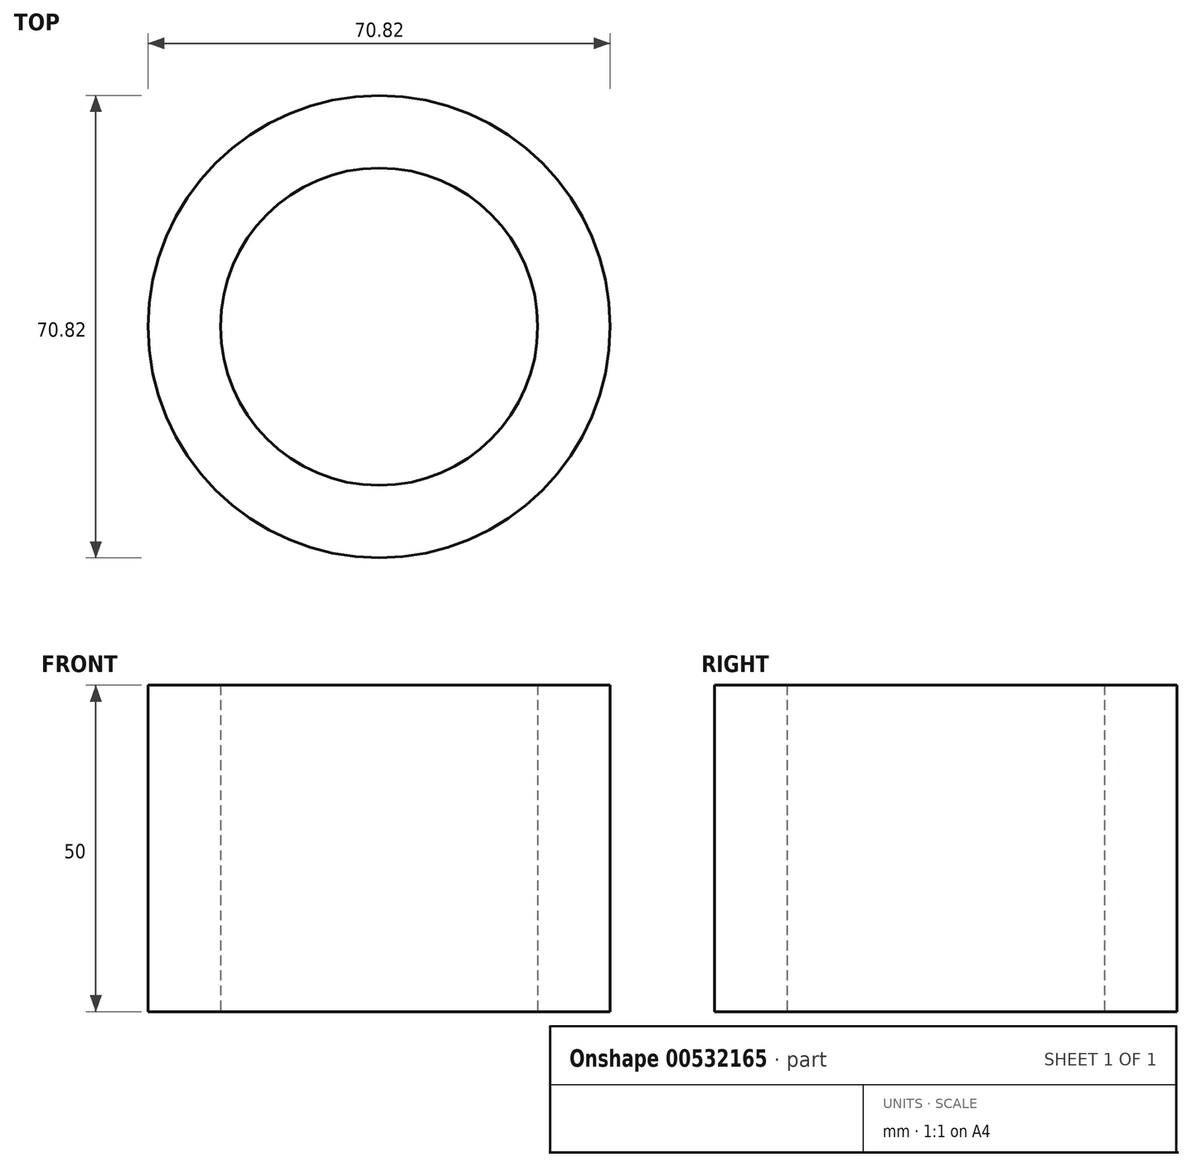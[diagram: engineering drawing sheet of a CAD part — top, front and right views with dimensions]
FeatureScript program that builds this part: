
annotation { "Feature Type Name" : "Feature", "Feature Type Description" : "" }
export const myFeature = defineFeature(function(context is Context, id is Id, definition is map)
    precondition{}
    {
        {
            var Q0;
            Q0=qCreatedBy(makeId("Top.planeOp"),FACE);
            var sketch = newSketch(context, id + "F0", { "sketchPlane" : qUnion([Q0])});
            skCircle(sketch, "E0", {"center": v(0, 0) * mm, "radius": 35.41 * mm});
            skSolve(sketch);
        }
        {
            var Q0;
            Q0 = qSketchRegion(id + "F0", true);
            extrude(context, id + "F1", {"entities" : qUnion([Q0]), "depth" : 50 * mm, "offsetDistance" : 25 * mm});
        }
        {
            var Q0;
            Q0=qCreatedBy(makeId("Top.planeOp"),FACE);
            var sketch = newSketch(context, id + "F2", { "sketchPlane" : qUnion([Q0])});
            skCircle(sketch, "E1", {"center": v(0, 0) * mm, "radius": 30.97 * mm});
            skSolve(sketch);
        }
        {
            var Q0;
            Q0 = qSketchRegion(id + "F2", true);
            extrude(context, id + "F3", {"entities" : qUnion([Q0]), "operationType" : NewBodyOperationType.REMOVE, "oppositeDirection" : true, "depth" : 50 * mm, "offsetDistance" : 25 * mm});
        }
        {
            var Q0;
            Q0=qCreatedBy(makeId("Top.planeOp"),FACE);
            var sketch = newSketch(context, id + "F4", { "sketchPlane" : qUnion([Q0])});
            skCircle(sketch, "E2", {"center": v(0, 0) * mm, "radius": 30.4 * mm});
            skSolve(sketch);
        }
        {
            var Q0;
            Q0 = qSketchRegion(id + "F4", true);
            extrude(context, id + "F5", {"entities" : qUnion([Q0]), "operationType" : NewBodyOperationType.REMOVE, "oppositeDirection" : true, "depth" : 50 * mm, "offsetDistance" : 25 * mm});
        }
        {
            var Q0;
            Q0=qCreatedBy(makeId("Top.planeOp"),FACE);
            var sketch = newSketch(context, id + "F6", { "sketchPlane" : qUnion([Q0])});
            skCircle(sketch, "E3", {"center": v(0, 0) * mm, "radius": 24.31 * mm});
            skSolve(sketch);
        }
        {
            var Q0;
            Q0 = qSketchRegion(id + "F6", true);
            extrude(context, id + "F7", {"entities" : qUnion([Q0]), "operationType" : NewBodyOperationType.REMOVE, "depth" : 50 * mm, "offsetDistance" : 25 * mm});
        }
    });
